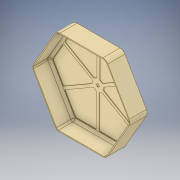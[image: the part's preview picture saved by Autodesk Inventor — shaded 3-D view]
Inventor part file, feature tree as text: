
AUTODESK INVENTOR PART (.ipt)
format: ipt  version: 2019 (Build 230136000, 136)  size: 544,768 bytes
history: native  units: mm
features: mirror x4, extrude x3, sketch x3, plane x3, fillet x3, projected_geometry x2, shell x1
ambient origin geometry x8: Origin, YZ Plane, XZ Plane, XY Plane, X Axis, Y Axis, Z Axis, Center Point
bodies: Solid1 (feature_tree)
feature tree (19):
  extrude  "Extrusion1"  Depth=30.0mm TaperAngle=0.0deg
  shell  "Shell1"  Thickness=1.5mm
  sketch  "Sketch2"  dims[d5=2.0mm d6=15.0mm]
  plane  "Work Plane1"
  plane  "Work Plane2"
  plane  "Work Plane3"
  extrude  "Extrusion5"  Depth=2.0mm
  extrude  "Extrusion2"  Depth=1.0mm TaperAngle=0.0deg
  mirror  "Mirror1"
  mirror  "Mirror2"
  mirror  "Mirror3"
  mirror  "Mirror4"
  fillet  "Fillet1"  Radius=4.0mm
  fillet  "Fillet2"  Radius=10.0mm
  fillet  "Fillet4"  Radius=1.0mm
  sketch  "Sketch1"  dims[d0=150.0mm d2=30.0mm d3=0.0mm d4=1.5mm]
  projected_geometry  "Projected Loop1"
  sketch  "Sketch4"  dims[d7=15.0mm d8=1.0mm d9=0.0mm d10=4.0mm d11=10.0mm d12=1.0mm d37=5.0mm d44=10.0mm d45=60.0deg d46=90.0deg d47=90.0deg d48=60.0mm d50=360.0deg d52=5.5mm d53=0.75mm d54=0.0mm d55=5.0mm d56=2.0mm]
  projected_geometry  "Projected Loop3"
